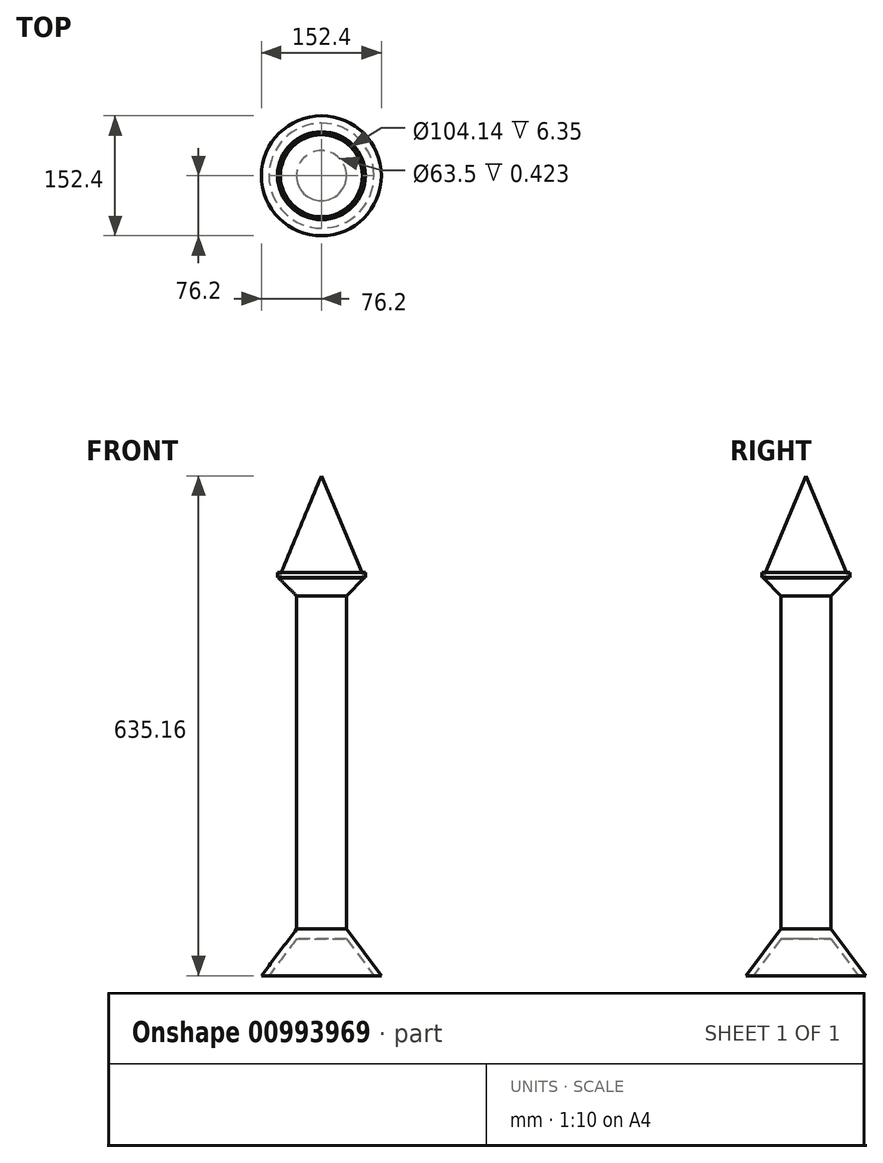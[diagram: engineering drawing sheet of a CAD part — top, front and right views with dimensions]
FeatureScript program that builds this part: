
annotation { "Feature Type Name" : "Feature", "Feature Type Description" : "" }
export const myFeature = defineFeature(function(context is Context, id is Id, definition is map)
    precondition{}
    {
        {
            var Q0;
            Q0=qCreatedBy(makeId("Front.planeOp"),FACE);
            var sketch = newSketch(context, id + "F0", { "sketchPlane" : qUnion([Q0])});
            skLineSegment(sketch, "E0", {"start": v(0, 101.6) * mm, "end": v(0, 0) * mm});
            skLineSegment(sketch, "E1", {"start": v(0, 101.6) * mm, "end": v(76.2, 0) * mm});
            skLineSegment(sketch, "E2", {"start": v(76.2, 0) * mm, "end": v(0, 0) * mm});
            skSolve(sketch);
        }
        {
            var Q0;
            Q0=makeQuery(id+"F0.imprint","IMPRINT",FACE,{"disambiguationData":[TD([[makeQuery(id+"F0.imprint","IMPRINT",EDGE,{"derivedFrom":sQuery(id+"F0.wireOp",EDGE,"E0")}),1.0]])]});
            var Q1;
            Q1=sQuery(id+"F0.wireOp",EDGE,"E0");
            revolve(context, id + "F1", {"surfaceOperationType" : NewSurfaceOperationType.NEW, "entities" : qUnion([Q0]), "axis" : qUnion([Q1]), "revolveType" : RevolveType.FULL});
        }
        {
            var Q0;
            Q0=makeQuery(id+"F1.opRevolve","SWEPT_FACE",FACE,{"disambiguationData":[OSD([sQuery(id+"F0.wireOp",EDGE,"E2")])]});
            shell(context, id + "F2", {"entities" : qUnion([Q0]), "thickness" : 7.62 * mm});
        }
        {
            var Q0;
            Q0=qCreatedBy(makeId("Top.planeOp"),FACE);
            var sketch = newSketch(context, id + "F3", { "sketchPlane" : qUnion([Q0])});
            skCircle(sketch, "E3", {"center": v(0, 0) * mm, "radius": 31.75 * mm});
            skSolve(sketch);
        }
        {
            var Q0;
            Q0=makeQuery(id+"F3.imprint","IMPRINT",FACE,{"disambiguationData":[TD([[makeQuery(id+"F3.imprint","IMPRINT",EDGE,{"derivedFrom":sQuery(id+"F3.wireOp",EDGE,"E3")}),1.0]])]});
            extrude(context, id + "F4", {"entities" : qUnion([Q0]), "operationType" : NewBodyOperationType.ADD, "depth" : 482.6 * mm, "offsetDistance" : 25.4 * mm, "hasSecondDirection" : true, "secondDirectionOppositeDirection" : false, "secondDirectionDepth" : 25.4 * mm});
        }
        {
            var Q0;
            Q0=makeQuery(id+"F4.opExtrude","CAP_FACE",FACE,{"disambiguationData":[OSD([sQuery(id+"F3.wireOp",EDGE,"E3")])],"isStart":false});
            var sketch = newSketch(context, id + "F5", { "sketchPlane" : qUnion([Q0])});
            skLineSegment(sketch, "E4.bottom", {"start": v(-1.27, 1.27) * mm, "end": v(1.27, 1.27) * mm});
            skLineSegment(sketch, "E4.top", {"start": v(-1.27, -1.27) * mm, "end": v(1.27, -1.27) * mm});
            skLineSegment(sketch, "E4.left", {"start": v(-1.27, 1.27) * mm, "end": v(-1.27, -1.27) * mm});
            skLineSegment(sketch, "E4.right", {"start": v(1.27, 1.27) * mm, "end": v(1.27, -1.27) * mm});
            skPoint(sketch, "E4.middle", {"position": v(0, 0) * mm});
            skSolve(sketch);
        }
        {
            var Q0;
            Q0=qCreatedBy(makeId("Front.planeOp"),FACE);
            var sketch = newSketch(context, id + "F6", { "sketchPlane" : qUnion([Q0])});
            skLineSegment(sketch, "E5", {"start": v(0, 482.76) * mm, "end": v(0, 635.16) * mm});
            skLineSegment(sketch, "E6", {"start": v(0, 482.76) * mm, "end": v(63.5, 482.76) * mm});
            skLineSegment(sketch, "E7", {"start": v(63.5, 482.76) * mm, "end": v(0, 635.16) * mm});
            skSolve(sketch);
        }
        {
            var Q0;
            Q0=makeQuery(id+"F6.imprint","IMPRINT",FACE,{"disambiguationData":[TD([[makeQuery(id+"F6.imprint","IMPRINT",EDGE,{"derivedFrom":sQuery(id+"F6.wireOp",EDGE,"E5")}),-1.0]])]});
            var Q1;
            Q1=sQuery(id+"F6.wireOp",EDGE,"E5");
            revolve(context, id + "F7", {"operationType" : NewBodyOperationType.ADD, "surfaceOperationType" : NewSurfaceOperationType.NEW, "entities" : qUnion([Q0]), "axis" : qUnion([Q1]), "revolveType" : RevolveType.FULL});
        }
        {
            var Q0;
            Q0=makeQuery(id+"F5.imprint","IMPRINT",FACE,{"disambiguationData":[TD([[makeQuery(id+"F5.imprint","IMPRINT",EDGE,{"derivedFrom":sQuery(id+"F5.wireOp",EDGE,"E4.bottom")}),1.0]])]});
            var sketch = newSketch(context, id + "F8", { "sketchPlane" : qUnion([Q0])});
            skCircle(sketch, "E8", {"center": v(0, 0) * mm, "radius": 55.88 * mm});
            skCircle(sketch, "E9", {"center": v(0, 0) * mm, "radius": 52.07 * mm});
            skSolve(sketch);
        }
        {
            var Q0;
            Q0=makeQuery(id+"F8.imprint","IMPRINT",FACE,{"disambiguationData":[TD([[makeQuery(id+"F8.imprint","IMPRINT",EDGE,{"derivedFrom":sQuery(id+"F8.wireOp",EDGE,"E8")}),1.0]])]});
            extrude(context, id + "F9", {"entities" : qUnion([Q0]), "depth" : 34.3 * mm, "offsetDistance" : 25.4 * mm, "hasSecondDirection" : true, "secondDirectionOppositeDirection" : false, "secondDirectionDepth" : 23.1 * mm});
        }
        {
            var Q0;
            Q0=makeQuery(id+"F7.opRevolve","SWEPT_EDGE",EDGE,{"disambiguationData":[OSD([sQuery(id+"F6.wireOp",EDGE,"E6"),sQuery(id+"F6.wireOp",EDGE,"E7")])]});
            chamfer(context, id + "F10", {"entities" : qUnion([Q0]), "chamferType" : ChamferType.OFFSET_ANGLE, "width" : 31.75 * mm, "oppositeDirection" : false, "angle" : 45 * degree, "tangentPropagation" : true});
        }
        {
            var Q0;
            Q0=makeQuery(id+"F9.opExtrude","CAP_FACE",FACE,{"disambiguationData":[OSD([sQuery(id+"F8.wireOp",EDGE,"E8"),sQuery(id+"F8.wireOp",EDGE,"E9")])],"isStart":false});
            extrude(context, id + "F11", {"entities" : qUnion([Q0]), "operationType" : NewBodyOperationType.REMOVE, "oppositeDirection" : true, "depth" : 4.83 * mm, "offsetDistance" : 25.4 * mm});
        }
        {
            var Q0;
            Q0=makeQuery(id+"F4.opExtrude","CAP_FACE",FACE,{"disambiguationData":[OSD([sQuery(id+"F3.wireOp",EDGE,"E3")])],"isStart":true});
            extrude(context, id + "F12", {"entities" : qUnion([Q0]), "operationType" : NewBodyOperationType.REMOVE, "oppositeDirection" : true, "depth" : 33.27 * mm, "offsetDistance" : 25.4 * mm});
        }
        {
            var Q0;
            Q0=makeQuery(id+"F12.boolean.opBoolean","COPY",FACE,{"derivedFrom":makeQuery(id+"F12.opExtrude","CAP_FACE",FACE,{"disambiguationData":[OSD([sQuery(id+"F3.wireOp",EDGE,"E3")])],"isStart":false})});
            extrude(context, id + "F13", {"entities" : qUnion([Q0]), "operationType" : NewBodyOperationType.ADD, "depth" : 11.68 * mm, "offsetDistance" : 25.4 * mm});
        }
    });
